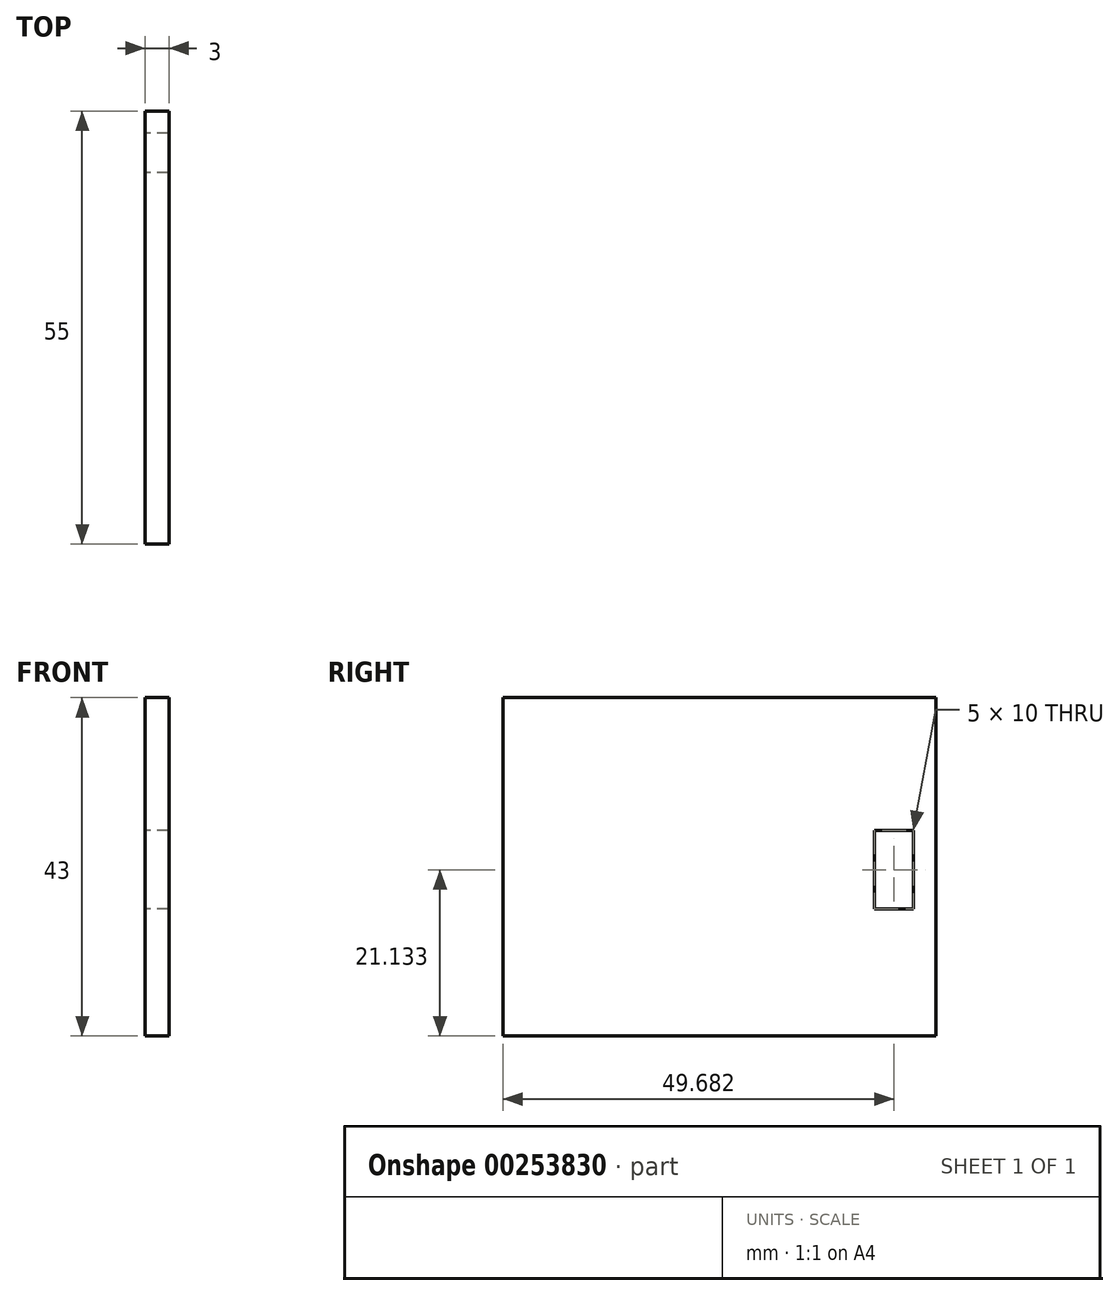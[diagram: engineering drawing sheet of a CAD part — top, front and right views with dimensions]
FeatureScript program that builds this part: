
annotation { "Feature Type Name" : "Feature", "Feature Type Description" : "" }
export const myFeature = defineFeature(function(context is Context, id is Id, definition is map)
    precondition{}
    {
        {
            var Q0;
            Q0=qCreatedBy(makeId("Right.planeOp"),FACE);
            var sketch = newSketch(context, id + "F0", { "sketchPlane" : qUnion([Q0])});
            skLineSegment(sketch, "E0", {"start": v(-27.5, -20) * mm, "end": v(27.5, -20) * mm});
            skLineSegment(sketch, "E1", {"start": v(27.5, -20) * mm, "end": v(27.5, 20) * mm});
            skLineSegment(sketch, "E2", {"start": v(27.5, 23) * mm, "end": v(-27.5, 23) * mm});
            skLineSegment(sketch, "E3", {"start": v(-27.5, 20) * mm, "end": v(-27.5, -20) * mm});
            skLineSegment(sketch, "E4", {"start": v(19.68, -3.87) * mm, "end": v(19.68, 6.13) * mm});
            skLineSegment(sketch, "E5", {"start": v(19.68, 6.13) * mm, "end": v(24.68, 6.13) * mm});
            skLineSegment(sketch, "E6", {"start": v(24.68, 6.13) * mm, "end": v(24.68, -3.87) * mm});
            skLineSegment(sketch, "E7", {"start": v(24.68, -3.87) * mm, "end": v(19.68, -3.87) * mm});
            skLineSegment(sketch, "E8", {"start": v(-27.5, 23) * mm, "end": v(-27.5, 20) * mm});
            skLineSegment(sketch, "E9", {"start": v(27.5, 23) * mm, "end": v(27.5, 20) * mm});
            skSolve(sketch);
        }
        {
            var Q0;
            Q0 = qSketchRegion(id + "F0", true);
            extrude(context, id + "F1", {"entities" : qUnion([Q0]), "depth" : 3 * mm});
        }
    });
